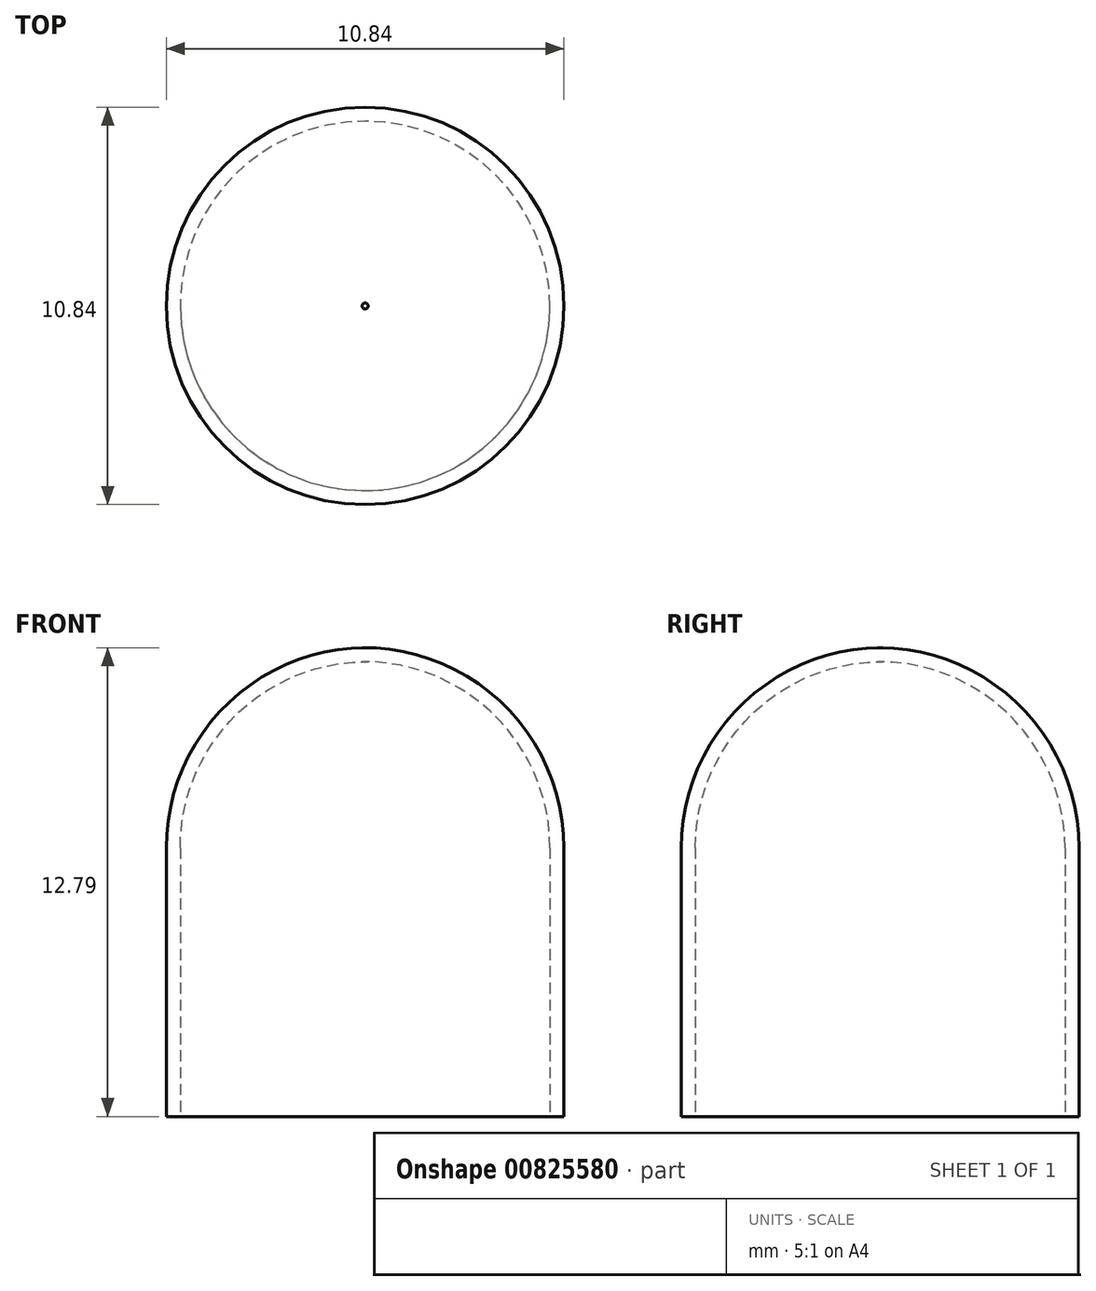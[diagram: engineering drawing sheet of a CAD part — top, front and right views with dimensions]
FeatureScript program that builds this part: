
annotation { "Feature Type Name" : "Feature", "Feature Type Description" : "" }
export const myFeature = defineFeature(function(context is Context, id is Id, definition is map)
    precondition{}
    {
        {
            var Q0;
            Q0=qCreatedBy(makeId("Front.planeOp"),FACE);
            var sketch = newSketch(context, id + "F0", { "sketchPlane" : qUnion([Q0])});
            skLineSegment(sketch, "E0", {"start": v(-0.04, 7.33) * mm, "end": v(0, 7.33) * mm});
            skLineSegment(sketch, "E1", {"start": v(5.04, 7.33) * mm, "end": v(5.04, 0) * mm});
            skLineSegment(sketch, "E2", {"start": v(5.04, 0) * mm, "end": v(5.42, 0) * mm});
            skLineSegment(sketch, "E3", {"start": v(5.42, 0) * mm, "end": v(5.42, 7.33) * mm});
            skLineSegment(sketch, "E4", {"start": v(5.42, 7.33) * mm, "end": v(5.04, 7.33) * mm});
            skArc(sketch, "E5", {"start": v(5.42, 7.33) * mm, "mid": v(3.84, 11.17) * mm, "end": v(0, 12.79) * mm});
            skArc(sketch, "E6", {"start": v(5.04, 7.33) * mm, "mid": v(3.57, 10.9) * mm, "end": v(0, 12.4) * mm});
            skLineSegment(sketch, "E7", {"start": v(0, 0) * mm, "end": v(0, 16.67) * mm, "construction": true});
            skLineSegment(sketch, "E8", {"start": v(0, 12.4) * mm, "end": v(0, 12.79) * mm});
            skPoint(sketch, "E8.startSnap0", {"position": v(-0.08, 12.4) * mm});
            skLineSegment(sketch, "E9", {"start": v(0, 12.79) * mm, "end": v(0, 12.4) * mm});
            skLineSegment(sketch, "E10.trimOffspring", {"start": v(0, 7.33) * mm, "end": v(-0.04, 7.33) * mm});
            skSolve(sketch);
        }
        {
            var Q0;
            {var subQ0=sQuery(id+"F0.wireOp",EDGE,"Knnb8tRt-JJSC-GeLf-JICp-eAvEMYMsdSDj");Q0=makeQuery(id+"F0.imprint","IMPRINT",FACE,{"disambiguationData":[TD([[makeQuery(id+"F0.imprint","IMPRINT",EDGE,{"derivedFrom":subQ0}),1.0]])]});}
            var Q1;
            {var subQ2=sQuery(id+"F0.wireOp",EDGE,"E5");Q1=makeQuery(id+"F0.imprint","IMPRINT",FACE,{"disambiguationData":[TD([[makeQuery(id+"F0.imprint","IMPRINT",EDGE,{"derivedFrom":subQ2}),1.0]])]});}
            var Q2;
            {var subQ0=sQuery(id+"F0.wireOp",EDGE,"E1");Q2=makeQuery(id+"F0.imprint","IMPRINT",FACE,{"disambiguationData":[TD([[makeQuery(id+"F0.imprint","IMPRINT",EDGE,{"derivedFrom":subQ0}),1.0]])]});}
            var Q3;
            Q3=sQuery(id+"F0.wireOp",EDGE,"E7");
            revolve(context, id + "F1", {"surfaceOperationType" : NewSurfaceOperationType.NEW, "entities" : qUnion([Q0, Q1, Q2]), "axis" : qUnion([Q3]), "revolveType" : RevolveType.FULL});
        }
    });
